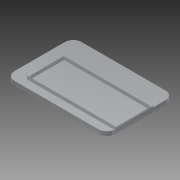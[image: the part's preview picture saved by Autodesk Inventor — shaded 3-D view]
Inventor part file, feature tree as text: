
AUTODESK INVENTOR PART (.ipt)
format: ipt  version: 2014 (Build 180170000, 170)  size: 130,560 bytes
history: native  units: mm
features: reference x12, extrude x2, sketch x2
ambient origin geometry x8: Origin, YZ Plane, XZ Plane, XY Plane, X Axis, Y Axis, Z Axis, Center Point
bodies: Solid1 (feature_tree)
feature tree (16):
  extrude  "Extrusion1"  Depth=51.0mm
  extrude  "Extrusion2"  Depth=53.0mm
  sketch  "Sketch1"  dims[d0=2.5mm d1=0.0mm d2=51.0mm]
  reference  "Reference1"
  reference  "Reference2"
  reference  "Reference3"
  reference  "Reference4"
  reference  "Reference5"
  reference  "Reference6"
  reference  "Reference7"
  reference  "Reference8"
  reference  "Reference9"
  reference  "Reference10"
  reference  "Reference11"
  reference  "Reference12"
  sketch  "Sketch2"  dims[d3=20.0mm d4=53.0mm d5=22.0mm d6=2.0mm d7=0.0mm d8=60.0mm d9=40.0mm]
